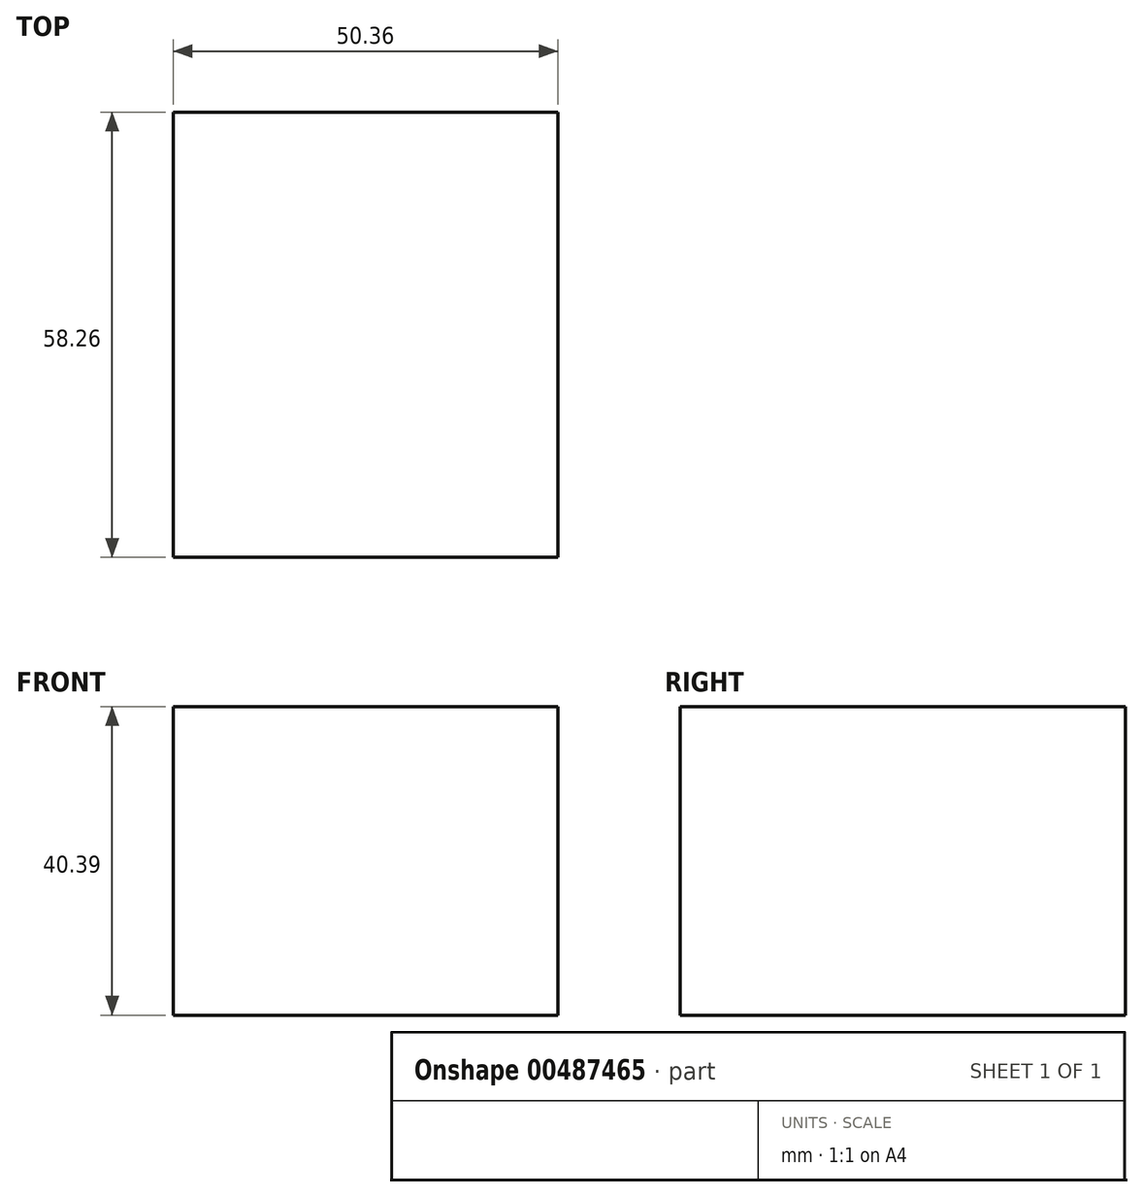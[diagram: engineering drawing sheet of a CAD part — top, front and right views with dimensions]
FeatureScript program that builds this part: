
annotation { "Feature Type Name" : "Feature", "Feature Type Description" : "" }
export const myFeature = defineFeature(function(context is Context, id is Id, definition is map)
    precondition{}
    {
        {
            var Q0;
            Q0=qCreatedBy(makeId("Top.planeOp"),FACE);
            var sketch = newSketch(context, id + "F0", { "sketchPlane" : qUnion([Q0])});
            skLineSegment(sketch, "E0.bottom", {"start": v(-25.18, -29.13) * mm, "end": v(25.18, -29.13) * mm});
            skLineSegment(sketch, "E0.top", {"start": v(-25.18, 29.13) * mm, "end": v(25.18, 29.13) * mm});
            skLineSegment(sketch, "E0.left", {"start": v(-25.18, -29.13) * mm, "end": v(-25.18, 29.13) * mm});
            skLineSegment(sketch, "E0.right", {"start": v(25.18, -29.13) * mm, "end": v(25.18, 29.13) * mm});
            skPoint(sketch, "E0.middle", {"position": v(0, 0) * mm});
            skSolve(sketch);
        }
        {
            var Q0;
            Q0 = qSketchRegion(id + "F0", true);
            extrude(context, id + "F1", {"entities" : qUnion([Q0]), "oppositeDirection" : true, "depth" : 40.4 * mm});
        }
    });
